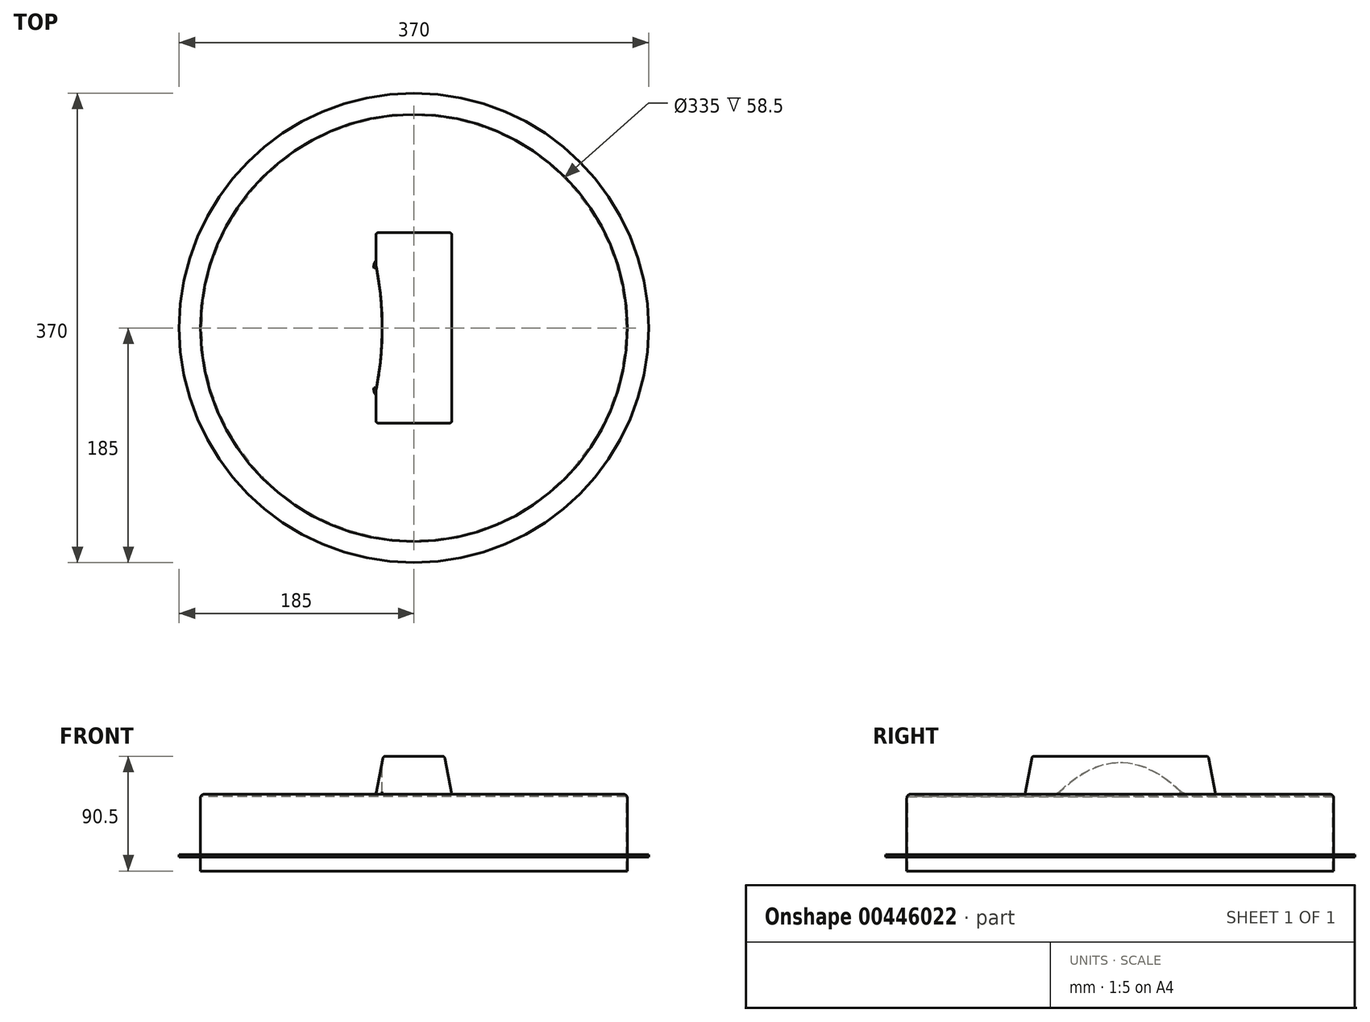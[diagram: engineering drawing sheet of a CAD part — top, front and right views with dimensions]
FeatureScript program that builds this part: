
annotation { "Feature Type Name" : "Feature", "Feature Type Description" : "" }
export const myFeature = defineFeature(function(context is Context, id is Id, definition is map)
    precondition{}
    {
        {
            var Q0;
            Q0=qCreatedBy(makeId("Top.planeOp"),FACE);
            var sketch = newSketch(context, id + "F0", { "sketchPlane" : qUnion([Q0])});
            skCircle(sketch, "E0", {"center": v(0, 0) * mm, "radius": 167.5 * mm});
            skCircle(sketch, "E1", {"center": v(0, 0) * mm, "radius": 168.25 * mm});
            skCircle(sketch, "E2", {"center": v(0, 0) * mm, "radius": 185 * mm});
            skSolve(sketch);
        }
        {
            var Q0;
            Q0=makeQuery(id+"F0.imprint","IMPRINT",FACE,{"disambiguationData":[TD([[makeQuery(id+"F0.imprint","IMPRINT",EDGE,{"derivedFrom":sQuery(id+"F0.wireOp",EDGE,"E0")}),-1.0]])]});
            extrude(context, id + "F1", {"entities" : qUnion([Q0]), "oppositeDirection" : true, "depth" : 11 * mm});
        }
        {
            var Q0;
            Q0=makeQuery(id+"F0.imprint","IMPRINT",FACE,{"disambiguationData":[TD([[makeQuery(id+"F0.imprint","IMPRINT",EDGE,{"derivedFrom":sQuery(id+"F0.wireOp",EDGE,"E0")}),-1.0]])]});
            var Q1;
            Q1=makeQuery(id+"F0.imprint","IMPRINT",FACE,{"disambiguationData":[TD([[makeQuery(id+"F0.imprint","IMPRINT",EDGE,{"derivedFrom":sQuery(id+"F0.wireOp",EDGE,"E1")}),-1.0]])]});
            extrude(context, id + "F2", {"entities" : qUnion([Q0, Q1]), "operationType" : NewBodyOperationType.ADD, "depth" : 2 * mm});
        }
        {
            var Q0;
            Q0=makeQuery(id+"F0.imprint","IMPRINT",FACE,{"disambiguationData":[TD([[makeQuery(id+"F0.imprint","IMPRINT",EDGE,{"derivedFrom":sQuery(id+"F0.wireOp",EDGE,"E0")}),-1.0]])]});
            extrude(context, id + "F3", {"entities" : qUnion([Q0]), "operationType" : NewBodyOperationType.ADD, "depth" : 47.5 * mm});
        }
        {
            var Q0;
            Q0=makeQuery(id+"F3.opExtrude","CAP_FACE",FACE,{"disambiguationData":[OSD([sQuery(id+"F0.wireOp",EDGE,"E0"),sQuery(id+"F0.wireOp",EDGE,"E1")])],"isStart":false});
            var sketch = newSketch(context, id + "F4", { "sketchPlane" : qUnion([Q0])});
            skCircle(sketch, "E3", {"center": v(0, 0) * mm, "radius": 168.25 * mm});
            skSolve(sketch);
        }
        {
            var Q0;
            Q0=makeQuery(id+"F4.imprint","IMPRINT",FACE,{"disambiguationData":[TD([[makeQuery(id+"F4.imprint","IMPRINT",EDGE,{"derivedFrom":makeQuery(id+"F3.opExtrude","CAP_EDGE",EDGE,{"disambiguationData":[OSD([sQuery(id+"F0.wireOp",EDGE,"E0")])],"isStart":false})}),1.0]])]});
            var Q1;
            Q1=makeQuery(id+"F4.imprint","IMPRINT",FACE,{"disambiguationData":[TD([[makeQuery(id+"F4.imprint","IMPRINT",EDGE,{"derivedFrom":sQuery(id+"F4.wireOp",EDGE,"E3")}),1.0]])]});
            extrude(context, id + "F5", {"entities" : qUnion([Q0, Q1]), "operationType" : NewBodyOperationType.ADD, "depth" : 2 * mm});
        }
        {
            var Q0;
            Q0=makeQuery(id+"F5.opExtrude","CAP_FACE",FACE,{"disambiguationData":[OSD([sQuery(id+"F4.wireOp",EDGE,"E3")])],"isStart":false});
            fillet(context, id + "F6", {"entities" : qUnion([Q0]), "radius" : 3 * mm, "tangentPropagation" : true, "allowEdgeOverflow" : false});
        }
        {
            var Q0;
            Q0=makeQuery(id+"F5.opExtrude","CAP_FACE",FACE,{"disambiguationData":[OSD([sQuery(id+"F4.wireOp",EDGE,"E3")])],"isStart":false});
            var sketch = newSketch(context, id + "F7", { "sketchPlane" : qUnion([Q0])});
            skLineSegment(sketch, "E4.bottom", {"start": v(-30, 75) * mm, "end": v(30, 75) * mm});
            skLineSegment(sketch, "E4.top", {"start": v(-30, -75) * mm, "end": v(30, -75) * mm});
            skLineSegment(sketch, "E4.left", {"start": v(-30, 75) * mm, "end": v(-30, -75) * mm});
            skLineSegment(sketch, "E4.right", {"start": v(30, 75) * mm, "end": v(30, -75) * mm});
            skLineSegment(sketch, "E5.bottom", {"start": v(-24, 69.5) * mm, "end": v(24, 69.5) * mm});
            skLineSegment(sketch, "E5.top", {"start": v(-24, -69.5) * mm, "end": v(24, -69.5) * mm});
            skLineSegment(sketch, "E5.left", {"start": v(-24, 69.5) * mm, "end": v(-24, -69.5) * mm});
            skLineSegment(sketch, "E5.right", {"start": v(24, 69.5) * mm, "end": v(24, -69.5) * mm});
            skSolve(sketch);
        }
        {
            var Q0;
            Q0=makeQuery(id+"F7.imprint","IMPRINT",FACE,{"disambiguationData":[TD([[makeQuery(id+"F7.imprint","IMPRINT",EDGE,{"derivedFrom":sQuery(id+"F7.wireOp",EDGE,"E5.bottom")}),-1.0]])]});
            extrude(context, id + "F8", {"entities" : qUnion([Q0]), "operationType" : NewBodyOperationType.ADD, "depth" : 30 * mm});
        }
        {
            var Q0;
            Q0=makeQuery(id+"F8.opExtrude","SWEPT_FACE",FACE,{"disambiguationData":[OSD([sQuery(id+"F7.wireOp",EDGE,"E5.top")])]});
            var sketch = newSketch(context, id + "F9", { "sketchPlane" : qUnion([Q0])});
            skLineSegment(sketch, "E6", {"start": v(-24, 79.5) * mm, "end": v(-30, 49.5) * mm});
            skLineSegment(sketch, "E7", {"start": v(24, 79.5) * mm, "end": v(30, 49.5) * mm});
            skLineSegment(sketch, "E8", {"start": v(-30, 49.5) * mm, "end": v(-24, 49.5) * mm});
            skLineSegment(sketch, "E9", {"start": v(24, 49.5) * mm, "end": v(30, 49.5) * mm});
            skSolve(sketch);
        }
        {
            var Q0;
            Q0=makeQuery(id+"F9.imprint","IMPRINT",FACE,{"disambiguationData":[TD([[makeQuery(id+"F9.imprint","IMPRINT",EDGE,{"derivedFrom":sQuery(id+"F9.wireOp",EDGE,"E6")}),1.0]])]});
            var Q1;
            Q1=makeQuery(id+"F9.imprint","IMPRINT",FACE,{"disambiguationData":[TD([[makeQuery(id+"F9.imprint","IMPRINT",EDGE,{"derivedFrom":sQuery(id+"F9.wireOp",EDGE,"E7")}),-1.0]])]});
            var Q2;
            Q2=makeQuery(id+"F8.opExtrude","SWEPT_FACE",FACE,{"disambiguationData":[OSD([sQuery(id+"F7.wireOp",EDGE,"E5.bottom")])]});
            extrude(context, id + "F10", {"entities" : qUnion([Q0, Q1]), "operationType" : NewBodyOperationType.ADD, "endBound" : BoundingType.UP_TO_SURFACE, "oppositeDirection" : true, "endBoundEntityFace" : qUnion([Q2]), "depth" : 25 * mm});
        }
        {
            var Q0;
            Q0=makeQuery(id+"F10.opExtrude","SWEPT_FACE",FACE,{"disambiguationData":[OSD([sQuery(id+"F9.wireOp",EDGE,"E6")])]});
            var sketch = newSketch(context, id + "F11", { "sketchPlane" : qUnion([Q0])});
            skLineSegment(sketch, "E10", {"start": v(-69.5, 73.25) * mm, "end": v(-75, 42.66) * mm});
            skLineSegment(sketch, "E11", {"start": v(-75, 42.66) * mm, "end": v(-69.5, 42.66) * mm});
            skLineSegment(sketch, "E12", {"start": v(69.5, 73.25) * mm, "end": v(75, 42.66) * mm});
            skLineSegment(sketch, "E13", {"start": v(75, 42.66) * mm, "end": v(69.5, 42.66) * mm});
            skSolve(sketch);
        }
        {
            var Q0;
            Q0=makeQuery(id+"F11.imprint","IMPRINT",FACE,{"disambiguationData":[TD([[makeQuery(id+"F11.imprint","IMPRINT",EDGE,{"derivedFrom":sQuery(id+"F11.wireOp",EDGE,"E10")}),1.0]])]});
            var Q1;
            Q1=makeQuery(id+"F11.imprint","IMPRINT",FACE,{"disambiguationData":[TD([[makeQuery(id+"F11.imprint","IMPRINT",EDGE,{"derivedFrom":sQuery(id+"F11.wireOp",EDGE,"E12")}),-1.0]])]});
            var Q2;
            Q2=makeQuery(id+"F8.opExtrude","CAP_EDGE",EDGE,{"disambiguationData":[OSD([sQuery(id+"F7.wireOp",EDGE,"E5.bottom")])],"isStart":false});
            sweep(context, id + "F12", {"operationType" : NewBodyOperationType.ADD, "profiles" : qUnion([Q0, Q1]), "path" : qUnion([Q2])});
        }
        {
            var Q0;
            Q0=makeQuery(id+"F10.opExtrude","SWEPT_FACE",FACE,{"disambiguationData":[OSD([sQuery(id+"F9.wireOp",EDGE,"E7")])]});
            var sketch = newSketch(context, id + "F13", { "sketchPlane" : qUnion([Q0])});
            skLineSegment(sketch, "E14", {"start": v(69.5, 73.25) * mm, "end": v(75, 42.66) * mm});
            skLineSegment(sketch, "E15", {"start": v(75, 42.66) * mm, "end": v(69.5, 42.66) * mm});
            skLineSegment(sketch, "E16", {"start": v(-69.5, 73.25) * mm, "end": v(-75, 42.66) * mm});
            skLineSegment(sketch, "E17", {"start": v(-75, 42.66) * mm, "end": v(-69.5, 42.66) * mm});
            skSolve(sketch);
        }
        {
            var Q0;
            Q0=makeQuery(id+"F13.imprint","IMPRINT",FACE,{"disambiguationData":[TD([[makeQuery(id+"F13.imprint","IMPRINT",EDGE,{"derivedFrom":sQuery(id+"F13.wireOp",EDGE,"E14")}),-1.0]])]});
            var Q1;
            Q1=makeQuery(id+"F13.imprint","IMPRINT",FACE,{"disambiguationData":[TD([[makeQuery(id+"F13.imprint","IMPRINT",EDGE,{"derivedFrom":sQuery(id+"F13.wireOp",EDGE,"E16")}),1.0]])]});
            var Q2;
            {var subQ0=sQuery(id+"F7.wireOp",EDGE,"E5.bottom");Q2=makeQuery(id+"F12.boolean.opBoolean","MERGE",EDGE,{"derivedFrom":[makeQuery(id+"F8.opExtrude","CAP_EDGE",EDGE,{"disambiguationData":[OSD([subQ0])],"isStart":false}),makeQuery(id+"F12.opSweep","SWEPT_EDGE",EDGE,{"disambiguationData":[OSD([subQ0,sQuery(id+"F7.wireOp",EDGE,"E5.top"),sQuery(id+"F7.wireOp",EDGE,"E5.left"),sQuery(id+"F9.wireOp",EDGE,"E6"),sQuery(id+"F11.wireOp",EDGE,"E10")])]})]});}
            sweep(context, id + "F14", {"operationType" : NewBodyOperationType.ADD, "profiles" : qUnion([Q0, Q1]), "path" : qUnion([Q2])});
        }
        {
            var Q0;
            Q0=makeQuery(id+"F8.opExtrude","CAP_FACE",FACE,{"disambiguationData":[OSD([sQuery(id+"F7.wireOp",EDGE,"E5.bottom"),sQuery(id+"F7.wireOp",EDGE,"E5.top"),sQuery(id+"F7.wireOp",EDGE,"E5.left"),sQuery(id+"F7.wireOp",EDGE,"E5.right")])],"isStart":false});
            var sketch = newSketch(context, id + "F15", { "sketchPlane" : qUnion([Q0])});
            skCircle(sketch, "E18", {"center": v(-275, 0) * mm, "radius": 250 * mm});
            skLineSegment(sketch, "E19", {"start": v(0, 0) * mm, "end": v(0, -220.37) * mm, "construction": true});
            skPoint(sketch, "E19.endSnap0", {"position": v(0, -69.5) * mm});
            skCircle(sketch, "E20.MirrorC", {"center": v(275, 0) * mm, "radius": 250 * mm});
            skSolve(sketch);
        }
        {
            var Q0;
            Q0=makeQuery(id+"F15.imprint","IMPRINT",FACE,{"disambiguationData":[TD([[makeQuery(id+"F15.imprint","IMPRINT",EDGE,{"derivedFrom":sQuery(id+"F15.wireOp",EDGE,"E18")}),1.0]])]});
            var Q1;
            Q1=makeQuery(id+"F15.imprint","IMPRINT",FACE,{"disambiguationData":[TD([[makeQuery(id+"F15.imprint","IMPRINT",EDGE,{"derivedFrom":sQuery(id+"F15.wireOp",EDGE,"E20.MirrorC")}),-1.0]])]});
            var Q2;
            Q2=makeQuery(id+"F5.opExtrude","CAP_FACE",FACE,{"disambiguationData":[OSD([sQuery(id+"F4.wireOp",EDGE,"E3")])],"isStart":false});
            extrude(context, id + "F16", {"entities" : qUnion([Q0, Q1]), "operationType" : NewBodyOperationType.REMOVE, "endBound" : BoundingType.UP_TO_SURFACE, "oppositeDirection" : true, "endBoundEntityFace" : qUnion([Q2]), "depth" : 25 * mm});
        }
        {
            var Q0;
            Q0=makeQuery(id+"F12.opSweep","CAP_EDGE",EDGE,{"disambiguationData":[OSD([sQuery(id+"F7.wireOp",EDGE,"E5.bottom"),sQuery(id+"F7.wireOp",EDGE,"E5.top"),sQuery(id+"F7.wireOp",EDGE,"E5.left"),sQuery(id+"F9.wireOp",EDGE,"E6"),sQuery(id+"F11.wireOp",EDGE,"E12")])],"isStart":true});
            var Q1;
            {var subQ0=sQuery(id+"F7.wireOp",EDGE,"E5.top");Q1=makeQuery(id+"F12.boolean.opBoolean","MERGE",EDGE,{"derivedFrom":[makeQuery(id+"F8.opExtrude","CAP_EDGE",EDGE,{"disambiguationData":[OSD([subQ0])],"isStart":false}),makeQuery(id+"F12.opSweep","SWEPT_EDGE",EDGE,{"disambiguationData":[OSD([sQuery(id+"F7.wireOp",EDGE,"E5.bottom"),subQ0,sQuery(id+"F7.wireOp",EDGE,"E5.left"),sQuery(id+"F9.wireOp",EDGE,"E6"),sQuery(id+"F11.wireOp",EDGE,"E12")])]})]});}
            var Q2;
            Q2=makeQuery(id+"F14.opSweep","CAP_EDGE",EDGE,{"disambiguationData":[OSD([sQuery(id+"F7.wireOp",EDGE,"E5.bottom"),sQuery(id+"F7.wireOp",EDGE,"E5.top"),sQuery(id+"F7.wireOp",EDGE,"E5.left"),sQuery(id+"F7.wireOp",EDGE,"E5.right"),sQuery(id+"F9.wireOp",EDGE,"E6"),sQuery(id+"F9.wireOp",EDGE,"E7"),sQuery(id+"F11.wireOp",EDGE,"E10"),sQuery(id+"F13.wireOp",EDGE,"E16")])],"isStart":true});
            var Q3;
            {var subQ0=sQuery(id+"F7.wireOp",EDGE,"E5.left");Q3=makeQuery(id+"F10.boolean.opBoolean","MERGE",EDGE,{"derivedFrom":[makeQuery(id+"F8.opExtrude","CAP_EDGE",EDGE,{"disambiguationData":[OSD([subQ0])],"isStart":false}),makeQuery(id+"F10.opExtrude","SWEPT_EDGE",EDGE,{"disambiguationData":[OSD([sQuery(id+"F7.wireOp",EDGE,"E5.top"),subQ0,sQuery(id+"F9.wireOp",EDGE,"E6")])]})]});}
            var Q4;
            Q4=makeQuery(id+"F12.opSweep","CAP_EDGE",EDGE,{"disambiguationData":[OSD([sQuery(id+"F7.wireOp",EDGE,"E5.bottom"),sQuery(id+"F7.wireOp",EDGE,"E5.top"),sQuery(id+"F7.wireOp",EDGE,"E5.left"),sQuery(id+"F9.wireOp",EDGE,"E6"),sQuery(id+"F11.wireOp",EDGE,"E10")])],"isStart":true});
            var Q5;
            {var subQ0=sQuery(id+"F9.wireOp",EDGE,"E6");var subQ1=sQuery(id+"F7.wireOp",EDGE,"E5.left");var subQ2=sQuery(id+"F7.wireOp",EDGE,"E5.top");var subQ3=sQuery(id+"F7.wireOp",EDGE,"E5.bottom");Q5=makeQuery(id+"F16.boolean.opBoolean","INTERSECT",EDGE,{"derivedFrom":[makeQuery(id+"F12.boolean.opBoolean","MERGE",FACE,{"derivedFrom":[makeQuery(id+"F10.opExtrude","SWEPT_FACE",FACE,{"disambiguationData":[OSD([subQ0])]}),makeQuery(id+"F12.opSweep","CAP_FACE",FACE,{"disambiguationData":[OSD([subQ3,subQ2,subQ1,subQ0,sQuery(id+"F11.wireOp",EDGE,"E10"),sQuery(id+"F11.wireOp",EDGE,"E11")])],"isStart":true}),makeQuery(id+"F12.opSweep","CAP_FACE",FACE,{"disambiguationData":[OSD([subQ3,subQ2,subQ1,subQ0,sQuery(id+"F11.wireOp",EDGE,"E12"),sQuery(id+"F11.wireOp",EDGE,"E13")])],"isStart":true})]}),makeQuery(id+"F16.opExtrude","SWEPT_FACE",FACE,{"disambiguationData":[OSD([sQuery(id+"F15.wireOp",EDGE,"E18")])]})]});}
            var Q6;
            {var subQ0=sQuery(id+"F7.wireOp",EDGE,"E5.right");Q6=makeQuery(id+"F10.boolean.opBoolean","MERGE",EDGE,{"derivedFrom":[makeQuery(id+"F8.opExtrude","CAP_EDGE",EDGE,{"disambiguationData":[OSD([subQ0])],"isStart":false}),makeQuery(id+"F10.opExtrude","SWEPT_EDGE",EDGE,{"disambiguationData":[OSD([sQuery(id+"F7.wireOp",EDGE,"E5.top"),subQ0,sQuery(id+"F9.wireOp",EDGE,"E7")])]})]});}
            var Q7;
            {var subQ0=sQuery(id+"F7.wireOp",EDGE,"E5.bottom");Q7=makeQuery(id+"F12.boolean.opBoolean","MERGE",EDGE,{"derivedFrom":[makeQuery(id+"F8.opExtrude","CAP_EDGE",EDGE,{"disambiguationData":[OSD([subQ0])],"isStart":false}),makeQuery(id+"F12.opSweep","SWEPT_EDGE",EDGE,{"disambiguationData":[OSD([subQ0,sQuery(id+"F7.wireOp",EDGE,"E5.top"),sQuery(id+"F7.wireOp",EDGE,"E5.left"),sQuery(id+"F9.wireOp",EDGE,"E6"),sQuery(id+"F11.wireOp",EDGE,"E10")])]})]});}
            var Q8;
            Q8=makeQuery(id+"F14.opSweep","CAP_EDGE",EDGE,{"disambiguationData":[OSD([sQuery(id+"F7.wireOp",EDGE,"E5.bottom"),sQuery(id+"F7.wireOp",EDGE,"E5.top"),sQuery(id+"F7.wireOp",EDGE,"E5.left"),sQuery(id+"F7.wireOp",EDGE,"E5.right"),sQuery(id+"F9.wireOp",EDGE,"E6"),sQuery(id+"F9.wireOp",EDGE,"E7"),sQuery(id+"F11.wireOp",EDGE,"E10"),sQuery(id+"F13.wireOp",EDGE,"E14")])],"isStart":true});
            var Q9;
            {var subQ0=sQuery(id+"F11.wireOp",EDGE,"E10");var subQ1=sQuery(id+"F9.wireOp",EDGE,"E7");var subQ2=sQuery(id+"F9.wireOp",EDGE,"E6");var subQ3=sQuery(id+"F7.wireOp",EDGE,"E5.right");var subQ4=sQuery(id+"F7.wireOp",EDGE,"E5.left");var subQ5=sQuery(id+"F7.wireOp",EDGE,"E5.top");var subQ6=sQuery(id+"F7.wireOp",EDGE,"E5.bottom");Q9=makeQuery(id+"F16.boolean.opBoolean","INTERSECT",EDGE,{"derivedFrom":[makeQuery(id+"F14.boolean.opBoolean","MERGE",FACE,{"derivedFrom":[makeQuery(id+"F10.opExtrude","SWEPT_FACE",FACE,{"disambiguationData":[OSD([subQ1])]}),makeQuery(id+"F14.opSweep","CAP_FACE",FACE,{"disambiguationData":[OSD([subQ6,subQ5,subQ4,subQ3,subQ2,subQ1,subQ0,sQuery(id+"F13.wireOp",EDGE,"E14"),sQuery(id+"F13.wireOp",EDGE,"E15")])],"isStart":true}),makeQuery(id+"F14.opSweep","CAP_FACE",FACE,{"disambiguationData":[OSD([subQ6,subQ5,subQ4,subQ3,subQ2,subQ1,subQ0,sQuery(id+"F13.wireOp",EDGE,"E16"),sQuery(id+"F13.wireOp",EDGE,"E17")])],"isStart":true})]}),makeQuery(id+"F16.opExtrude","SWEPT_FACE",FACE,{"disambiguationData":[OSD([sQuery(id+"F15.wireOp",EDGE,"E20.MirrorC")])]})]});}
            var Q10;
            Q10=makeQuery(id+"F16.boolean.opBoolean","COPY",EDGE,{"derivedFrom":makeQuery(id+"F16.opExtrude","CAP_EDGE",EDGE,{"disambiguationData":[OSD([sQuery(id+"F15.wireOp",EDGE,"E20.MirrorC")])],"isStart":false})});
            var Q11;
            Q11=makeQuery(id+"F16.boolean.opBoolean","COPY",EDGE,{"derivedFrom":makeQuery(id+"F16.opExtrude","CAP_EDGE",EDGE,{"disambiguationData":[OSD([sQuery(id+"F15.wireOp",EDGE,"E18")])],"isStart":false})});
            fillet(context, id + "F17", {"entities" : qUnion([Q0, Q1, Q2, Q3, Q4, Q5, Q6, Q7, Q8, Q9, Q10, Q11]), "radius" : 2 * mm, "tangentPropagation" : true, "allowEdgeOverflow" : false});
        }
    });
